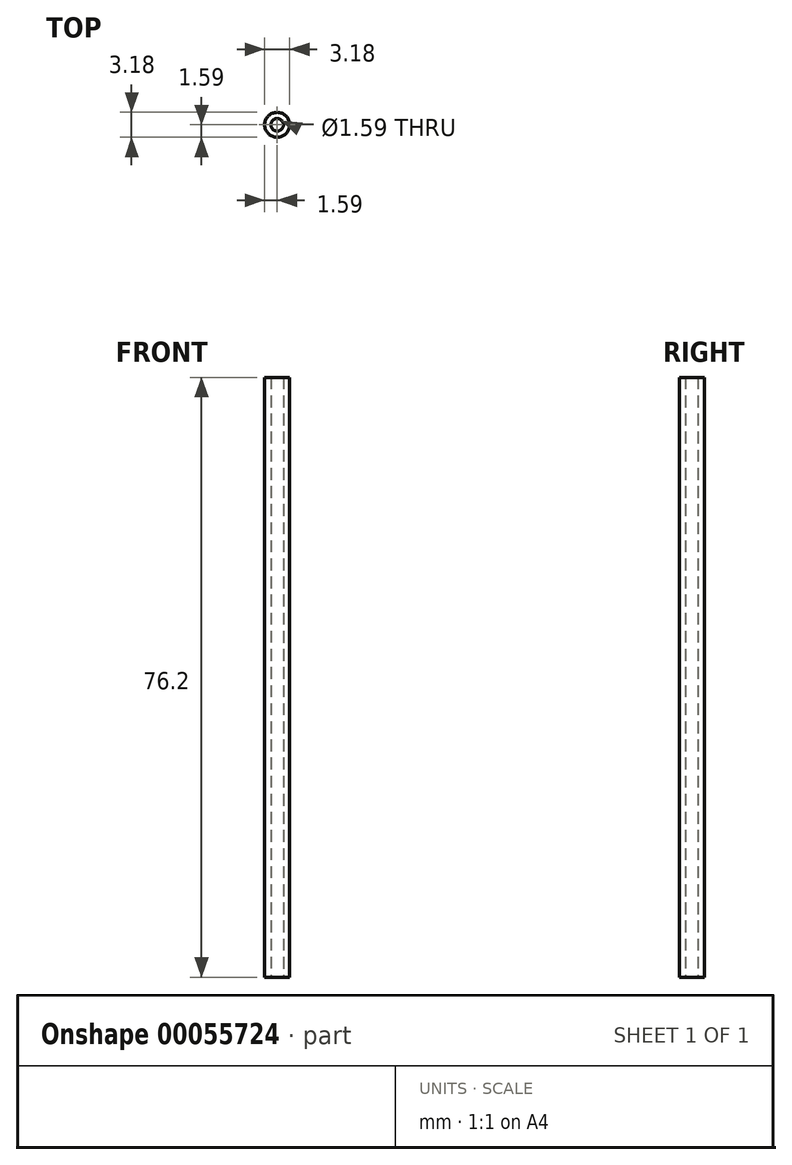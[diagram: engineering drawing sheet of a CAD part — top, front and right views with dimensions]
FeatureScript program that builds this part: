
annotation { "Feature Type Name" : "Feature", "Feature Type Description" : "" }
export const myFeature = defineFeature(function(context is Context, id is Id, definition is map)
    precondition{}
    {
        {
            var Q0;
            Q0=qCreatedBy(makeId("Top.planeOp"),FACE);
            var sketch = newSketch(context, id + "F0", { "sketchPlane" : qUnion([Q0])});
            skCircle(sketch, "E0", {"center": v(0, 0) * mm, "radius": 1.59 * mm});
            skCircle(sketch, "E1", {"center": v(0, 0) * mm, "radius": 0.8 * mm});
            skSolve(sketch);
        }
        {
            var Q0;
            Q0 = qSketchRegion(id + "F0", true);
            extrude(context, id + "F1", {"entities" : qUnion([Q0]), "depth" : 76.2 * mm});
        }
    });
